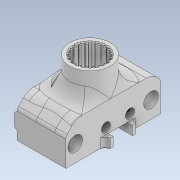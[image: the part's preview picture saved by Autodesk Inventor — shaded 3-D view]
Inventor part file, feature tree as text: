
AUTODESK INVENTOR PART (.ipt)
format: ipt  version: 2022.1 (Build 261234020, 234B)  size: 3,596,800 bytes
history: native  units: mm
features: projected_geometry x39, sketch x28, extrude x24, other x24, chamfer x12, delete_face x12, fillet x8, move_body x8, direct_edit x7, reference x5, hole x3
ambient origin geometry x8: Origin, YZ Plane, XZ Plane, XY Plane, X Axis, Y Axis, Z Axis, Center Point
bodies: Volumenkörper1 (feature_tree)
feature tree (170):
  extrude  "Extrusion1"  Depth=16.0mm
  extrude  "Extrusion2"  Depth=12.4mm TaperAngle=0.0deg
  other  "Verdickung21"
  other  "Verdickung22"
  other  "Verdickung23"
  other  "Verdickung24"
  other  "Verdickung25"
  other  "Verdickung26"
  other  "Verdickung27"
  other  "Verdickung28"
  other  "Verdickung29"
  other  "Verdickung30"
  other  "Verdickung31"
  other  "Verdickung32"
  other  "Verdickung33"
  other  "Verdickung34"
  other  "Verdickung35"
  other  "Verdickung36"
  other  "Verdickung37"
  other  "Verdickung38"
  other  "Verdickung39"
  other  "Verdickung40"
  extrude  "Extrusion4"  Depth=0.1mm
  hole  "Bohrung1"  [1 undecoded]
  extrude  "Extrusion5"  Depth=0.1mm
  chamfer  "Fase3"  Distance=0.1mm
  extrude  "Extrusion6"  Depth=1.0mm
  extrude  "Extrusion7"  Depth=1.0mm
  extrude  "Extrusion8"  Depth=1.0mm
  extrude  "Extrusion9"  Depth=1.0mm
  extrude  "Extrusion10"  Depth=1.0mm
  fillet  "Rundung1"  Radius=0.1mm
  hole  "Bohrung2"  [1 undecoded]
  extrude  "Extrusion11"  Depth=1.0mm
  chamfer  "Fase4"  Distance=0.1mm
  extrude  "Extrusion12"  Depth=1.0mm
  extrude  "Extrusion13"  Depth=1.0mm
  chamfer  "Fase5"  Distance=0.2mm
  direct_edit  "Direktbearbeitung1"
  hole  "Bohrung3"  [1 undecoded]
  direct_edit  "Direktbearbeitung2"
  extrude  "Extrusion14"  Depth=14.2mm TaperAngle=0.0deg
  chamfer  "Fase7"  Distance=2.0mm
  direct_edit  "Direktbearbeitung3"
  direct_edit  "Direktbearbeitung4"
  delete_face  "Fläche löschen1"
  extrude  "Extrusion15"  Depth=1.0mm TaperAngle=45.0deg
  delete_face  "Fläche löschen2"
  direct_edit  "Direktbearbeitung6"
  chamfer  "Fase8"  Distance=1.0mm
  sketch  "Skizze21"  dims[d70=0.1mm]
  delete_face  "Fläche löschen3"
  extrude  "Extrusion16"  TaperAngle=0.0deg  [1 undecoded]
  chamfer  "Fase9"  Distance=1.0mm
  delete_face  "Fläche löschen4"
  extrude  "Extrusion17"  Depth=1.0mm
  fillet  "Rundung5"  Radius=7.6mm
  fillet  "Rundung6"  Radius=6.4mm
  chamfer  "Fase10"  Distance=6.3mm
  fillet  "Rundung7"  Radius=4.0mm
  chamfer  "Fase11"  Distance=1.21mm
  delete_face  "Fläche löschen5"
  delete_face  "Fläche löschen6"
  extrude  "Extrusion18"  Depth=1.0mm
  extrude  "Extrusion19"  Depth=1.0mm
  chamfer  "Fase12"  Distance=4.0mm
  delete_face  "Fläche löschen7"
  extrude  "Extrusion20"  Depth=1.0mm
  extrude  "Extrusion21"  Depth=1.0mm
  delete_face  "Fläche löschen8"
  delete_face  "Fläche löschen9"
  extrude  "Extrusion22"  Depth=1.0mm
  delete_face  "Fläche löschen10"
  fillet  "Rundung8"  Radius=2.935mm
  fillet  "Rundung9"  Radius=2.935mm
  extrude  "Extrusion23"  Depth=1.0mm
  direct_edit  "Direktbearbeitung8"
  direct_edit  "Direktbearbeitung9"
  fillet  "Rundung10"  Radius=6.3mm
  fillet  "Rundung11"  Radius=3.15mm
  extrude  "Extrusion24"  Depth=1.0mm
  chamfer  "Fase13"  Distance=3.15mm
  chamfer  "Fase14"  Distance=4.225mm
  delete_face  "Fläche löschen11"
  delete_face  "Fläche löschen12"
  chamfer  "Fase15"  Distance=2.1125mm
  extrude  "Extrusion25"  Depth=1.0mm TaperAngle=0.0deg
  sketch  "Skizze1"  dims[d0=12.4mm d1=16.0mm]
  sketch  "Skizze2"  dims[d2=12.4mm d3=0.0mm d4=12.4mm d5=0.0mm]
  projected_geometry  "Projizierte Kontur1"
  sketch  "Skizze4"  dims[d52=0.1mm d53=0.1mm]
  reference  "Referenz1"
  projected_geometry  "Projizierte Kontur3"
  sketch  "Skizze5"  dims[d54=0.1mm d55=0.1mm]
  reference  "Referenz2"
  reference  "Referenz3"
  sketch  "Skizze7"  dims[d56=0.1mm d57=0.1mm]
  projected_geometry  "Projizierte Kontur7"
  projected_geometry  "Projizierte Kontur8"
  projected_geometry  "Projizierte Kontur9"
  sketch  "Skizze8"  dims[d58=0.1mm]
  projected_geometry  "Projizierte Kontur10"
  projected_geometry  "Projizierte Kontur11"
  sketch  "Skizze9"  dims[d59=0.1mm]
  projected_geometry  "Projizierte Kontur12"
  sketch  "Skizze10"  dims[d60=0.1mm]
  projected_geometry  "Projizierte Kontur13"
  projected_geometry  "Projizierte Kontur14"
  projected_geometry  "Projizierte Kontur15"
  sketch  "Skizze11"  dims[d61=0.1mm]
  projected_geometry  "Projizierte Kontur16"
  sketch  "Skizze12"  dims[d62=0.1mm]
  projected_geometry  "Projizierte Kontur17"
  projected_geometry  "Projizierte Kontur18"
  sketch  "Skizze13"  dims[d63=0.1mm]
  projected_geometry  "Projizierte Kontur19"
  projected_geometry  "Projizierte Kontur20"
  sketch  "Skizze14"  dims[d64=0.1mm]
  projected_geometry  "Projizierte Kontur21"
  sketch  "Skizze15"  dims[d65=0.1mm]
  projected_geometry  "Projizierte Kontur22"
  projected_geometry  "Projizierte Kontur23"
  sketch  "Skizze16"  dims[d66=0.1mm]
  projected_geometry  "Projizierte Kontur24"
  sketch  "Skizze18"  dims[d67=0.1mm]
  projected_geometry  "Projizierte Kontur25"
  projected_geometry  "Projizierte Kontur26"
  sketch  "Skizze19"  dims[d68=0.1mm]
  projected_geometry  "Projizierte Kontur27"
  sketch  "Skizze20"  dims[d69=0.1mm]
  projected_geometry  "Projizierte Kontur28"
  sketch  "Skizze22"  dims[d71=0.1mm]
  projected_geometry  "Projizierte Kontur29"
  sketch  "Skizze23"  dims[d72=0.1mm]
  projected_geometry  "Projizierte Kontur30"
  sketch  "Skizze24"  dims[d73=0.1mm]
  projected_geometry  "Projizierte Kontur31"
  projected_geometry  "Projizierte Kontur32"
  projected_geometry  "Projizierte Kontur33"
  sketch  "Skizze25"  dims[d74=0.1mm]
  projected_geometry  "Projizierte Kontur34"
  projected_geometry  "Projizierte Kontur35"
  projected_geometry  "Projizierte Kontur36"
  projected_geometry  "Projizierte Kontur37"
  sketch  "Skizze26"  dims[d75=0.1mm]
  projected_geometry  "Projizierte Kontur38"
  sketch  "Skizze27"  dims[d76=0.1mm]
  projected_geometry  "Projizierte Kontur39"
  sketch  "Skizze28"  dims[d77=0.1mm]
  projected_geometry  "Projizierte Kontur40"
  projected_geometry  "Projizierte Kontur41"
  sketch  "Skizze29"  dims[d78=0.1mm]
  reference  "Referenz4"
  reference  "Referenz5"
  sketch  "Skizze30"  dims[d79=0.1mm]
  projected_geometry  "Projizierte Kontur42"
  sketch  "Skizze31"  dims[d80=0.1mm d81=0.1mm d82=0.1mm d83=0.1mm d84=0.1mm d85=0.1mm d86=0.1mm d87=0.1mm d88=0.1mm d89=0.1mm d90=0.1mm d91=0.1mm d92=0.2mm d93=0.2mm d94=0.2mm d95=14.2mm d96=0.0mm d97=1.82mm d98=6.0mm d99=3.6mm d100=7.0mm d101=90.0deg d102=8.0mm d103=20.594885mm d107=2.0mm d108=0.0mm d112=0.4mm d113=2.0mm d114=45.0deg d115=1.0mm d116=0.0mm d117=0.0mm d118=0.0mm d119=1.0mm d120=0.0mm d125=7.0mm d126=7.6mm d127=6.4mm d128=6.3mm d129=4.0mm d130=0.0mm d131=1.21mm d132=1.21mm d133=7.0mm d134=4.0mm d135=0.0mm d136=2.0mm d137=3.375mm d138=3.375mm d139=2.935mm d140=2.935mm d141=5.025mm d142=6.3mm d143=3.15mm d144=2.5125mm d145=3.15mm d146=4.225mm d147=2.1125mm d148=1.7mm d149=6.0mm d150=3.6mm d151=7.0mm d152=90.0deg d153=8.0mm d154=20.594885mm d155=0.01mm d156=0.0mm d157=1.0mm d158=2.0mm d159=45.0deg d162=0.2mm d163=1.21mm d164=0.01mm d165=0.0mm d166=3.0mm d167=20.0mm d168=5.8mm d169=7.1mm d170=7.1mm d171=1.0mm d172=0.0mm d173=0.5mm d174=2.0mm d175=45.0deg d176=0.0mm d177=0.0mm d178=5.0mm d179=0.0mm d180=0.0mm d181=5.0mm d182=4.8mm d183=2.4mm d184=2.4mm d186=3.2mm d187=3.2mm d188=1.21mm d190=2.81mm d191=2.81mm d192=3.2mm d193=6.0mm d194=5.8mm d195=3.0mm d196=90.0deg d197=5.0mm d198=20.594885mm d199=0.0mm d200=0.0mm d201=1.25mm d202=0.8mm d203=0.8mm d204=0.0mm d205=0.0mm d210=0.4mm d211=2.0mm d212=45.0deg d213=0.0mm d214=0.0mm d215=-2.0mm d216=0.0mm d217=0.0mm d218=-0.5mm d219=10.0mm d220=0.0mm d224=0.0mm d225=0.0mm d226=-0.999mm d227=1.0mm d228=2.0mm d229=45.0deg d233=1.0mm d234=0.0mm d235=1.0mm d236=2.0mm d237=45.0deg d238=1.0mm d239=0.0mm d240=6.0mm d241=5.0mm d242=4.0mm d243=2.0mm d244=45.0deg d245=2.0mm d246=1.0mm d247=2.0mm d248=45.0deg d249=3.2mm d250=0.0mm d251=3.2mm d252=0.0mm d253=1.0mm d254=2.0mm d255=45.0deg d256=3.2mm d257=0.0mm d258=0.001mm d259=0.0mm d260=0.2mm d261=0.0mm d262=6.0mm d263=6.0mm d264=0.0mm d265=0.0mm d266=0.0mm d267=0.0mm d268=-0.39999mm d269=0.0mm d270=0.0mm d271=-0.4mm d272=2.0mm d273=0.4mm d274=1.0mm d275=0.0mm d276=0.4mm d277=2.0mm d278=45.0deg d279=0.4mm d280=2.0mm d281=45.0deg d282=0.4mm d283=2.0mm d284=45.0deg d285=1.0mm d286=0.0mm]
  projected_geometry  "Projizierte Kontur43"
  other  "<userpath>\Desktop\RAMA_SBNG\z_Endstop\Baugruppe1.iam"
  other  "Baugruppe1.iam"
  other  "MicroswitchBig:1"
  move_body  "Verschieben1"
  move_body  "Verschieben2"
  move_body  "Verschieben3"
  move_body  "Verschieben4"
  move_body  "Verschieben5"
  move_body  "Verschieben7"
  other  "Block:1"
  move_body  "Verschieben9"
  move_body  "Verschieben10"
note: 4 required parameter values undecoded (feature->parameter linkage not recoverable at this tier; creation-order binding heuristic only, values carry confidence <= 0.55)
